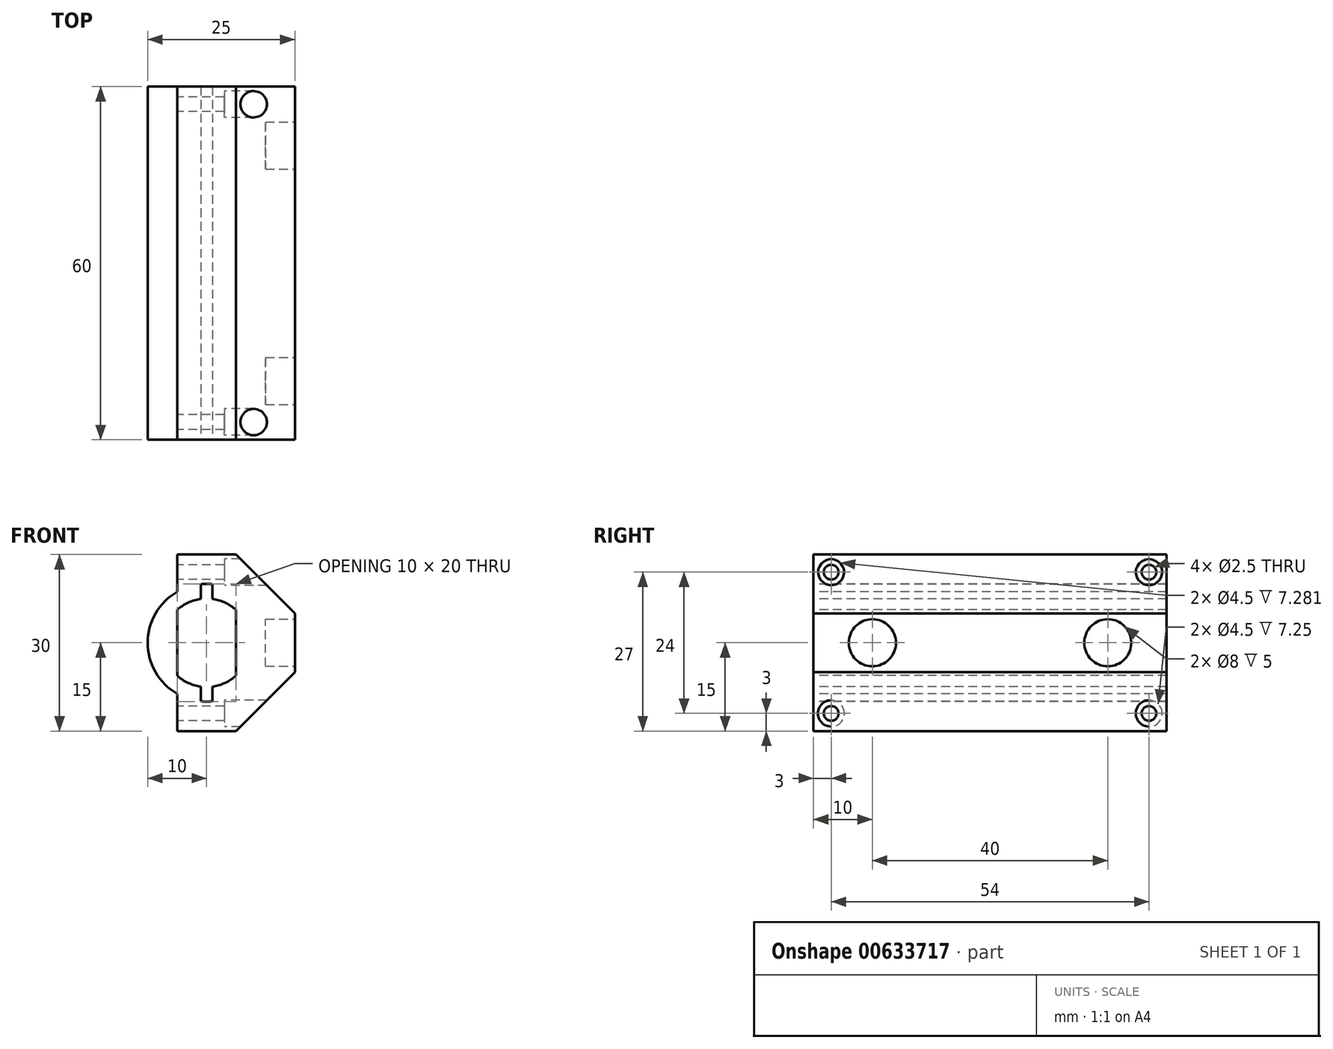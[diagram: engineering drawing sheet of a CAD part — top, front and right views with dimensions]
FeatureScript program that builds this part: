
annotation { "Feature Type Name" : "Feature", "Feature Type Description" : "" }
export const myFeature = defineFeature(function(context is Context, id is Id, definition is map)
    precondition{}
    {
        {
            var Q0;
            Q0=qCreatedBy(makeId("Right.planeOp"),FACE);
            var sketch = newSketch(context, id + "F0", { "sketchPlane" : qUnion([Q0])});
            skCircle(sketch, "E0", {"center": v(0, 0) * mm, "radius": 4 * mm});
            skSolve(sketch);
        }
        {
            var Q0;
            Q0 = qSketchRegion(id + "F0", true);
            extrude(context, id + "F1", {"entities" : qUnion([Q0]), "depth" : 200 * mm, "offsetDistance" : 25 * mm});
        }
        {
            var Q0;
            Q0=makeQuery(id+"F1.opExtrude","SWEPT_BODY",BODY,{"disambiguationData":[OSD([sQuery(id+"F0.wireOp",EDGE,"E0")])]});
            transform(context, id + "F2", {"entities" : qUnion([Q0]), "transformType" : TransformType.TRANSLATION_3D, "dx" : 0 * mm, "dy" : -40 * mm, "dz" : 0 * mm, "makeCopy" : true});
        }
        {
            var Q0;
            Q0=makeQuery(id+"F2.opPattern","COPY",FACE,{"derivedFrom":makeQuery(id+"F1.opExtrude","CAP_FACE",FACE,{"disambiguationData":[OSD([sQuery(id+"F0.wireOp",EDGE,"E0")])],"isStart":true}),"instanceName":"1"});
            var sketch = newSketch(context, id + "F3", { "sketchPlane" : qUnion([Q0])});
            skCircle(sketch, "E1", {"center": v(40, 0) * mm, "radius": 4 * mm});
            skCircle(sketch, "E2", {"center": v(0, 0) * mm, "radius": 4 * mm});
            skCircle(sketch, "E3", {"center": v(0, 0) * mm, "radius": 5 * mm});
            skCircle(sketch, "E4", {"center": v(40, 0) * mm, "radius": 5 * mm});
            skLineSegment(sketch, "E5", {"start": v(0, 0) * mm, "end": v(40, 0) * mm, "construction": true});
            skLineSegment(sketch, "E6", {"start": v(40, 5) * mm, "end": v(0, 5) * mm, "construction": true});
            skLineSegment(sketch, "E7", {"start": v(0, 5) * mm, "end": v(0, -5) * mm, "construction": true});
            skLineSegment(sketch, "E8", {"start": v(0, -5) * mm, "end": v(40, -5) * mm, "construction": true});
            skLineSegment(sketch, "E9", {"start": v(20, 5) * mm, "end": v(20, -5) * mm, "construction": true});
            skLineSegment(sketch, "E10.bottom", {"start": v(50, -15) * mm, "end": v(-10, -15) * mm});
            skLineSegment(sketch, "E10.top", {"start": v(50, 15) * mm, "end": v(-10, 15) * mm});
            skLineSegment(sketch, "E10.left", {"start": v(50, -15) * mm, "end": v(50, 15) * mm});
            skLineSegment(sketch, "E10.right", {"start": v(-10, -15) * mm, "end": v(-10, 15) * mm});
            skPoint(sketch, "E10.middle", {"position": v(20, 0) * mm});
            skSolve(sketch);
        }
        {
            var Q0;
            Q0=makeQuery(id+"F3.imprint","IMPRINT",FACE,{"disambiguationData":[TD([[makeQuery(id+"F3.imprint","IMPRINT",EDGE,{"derivedFrom":sQuery(id+"F3.wireOp",EDGE,"E1")}),1.0]])]});
            var Q1;
            Q1=makeQuery(id+"F3.imprint","IMPRINT",FACE,{"disambiguationData":[TD([[makeQuery(id+"F3.imprint","IMPRINT",EDGE,{"derivedFrom":sQuery(id+"F3.wireOp",EDGE,"E2")}),-1.0]])]});
            var Q2;
            Q2=sQuery(id+"F3.wireOp",EDGE,"E4");
            extrude(context, id + "F4", {"entities" : qUnion([Q0, Q1]), "surfaceEntities" : qUnion([Q2]), "oppositeDirection" : true, "depth" : 5 * mm, "offsetDistance" : 25 * mm});
        }
        {
            var Q0;
            Q0 = qSketchRegion(id + "F3", true);
            var Q1;
            Q1=makeQuery(id+"F4.opExtrude","CAP_FACE",FACE,{"disambiguationData":[OSD([sQuery(id+"F3.wireOp",EDGE,"E2"),sQuery(id+"F3.wireOp",EDGE,"E3")])],"isStart":true});
            var Q2;
            Q2=makeQuery(id+"F1.opExtrude","CAP_FACE",FACE,{"disambiguationData":[OSD([sQuery(id+"F0.wireOp",EDGE,"E0")])],"isStart":true});
            var Q3;
            Q3=makeQuery(id+"F2.opPattern","COPY",FACE,{"derivedFrom":makeQuery(id+"F1.opExtrude","CAP_FACE",FACE,{"disambiguationData":[OSD([sQuery(id+"F0.wireOp",EDGE,"E0")])],"isStart":true}),"instanceName":"1"});
            var Q4;
            Q4=makeQuery(id+"F4.opExtrude","CAP_FACE",FACE,{"disambiguationData":[OSD([sQuery(id+"F3.wireOp",EDGE,"E1"),sQuery(id+"F3.wireOp",EDGE,"E4")])],"isStart":true});
            extrude(context, id + "F5", {"entities" : qUnion([Q0, Q1, Q2, Q3, Q4]), "operationType" : NewBodyOperationType.ADD, "depth" : 30 * mm, "offsetDistance" : 25 * mm});
        }
        {
            var Q0;
            Q0=makeQuery(id+"F5.opExtrude","SWEPT_FACE",FACE,{"disambiguationData":[OSD([sQuery(id+"F3.wireOp",EDGE,"E10.left")])]});
            var sketch = newSketch(context, id + "F6", { "sketchPlane" : qUnion([Q0])});
            skCircle(sketch, "E11", {"center": v(-15, 0) * mm, "radius": 7.5 * mm});
            skPoint(sketch, "E11.centerSnap0", {"position": v(-15, 15) * mm});
            skCircle(sketch, "E12", {"center": v(-15, 0) * mm, "radius": 10 * mm});
            skLineSegment(sketch, "E13.bottom", {"start": v(-10, -15) * mm, "end": v(-20, -15) * mm});
            skLineSegment(sketch, "E13.top", {"start": v(-10, 15) * mm, "end": v(-20, 15) * mm});
            skLineSegment(sketch, "E13.left", {"start": v(-10, -15) * mm, "end": v(-10, 15) * mm});
            skLineSegment(sketch, "E13.right", {"start": v(-20, -15) * mm, "end": v(-20, 15) * mm});
            skLineSegment(sketch, "E14.bottom", {"start": v(-14, 15) * mm, "end": v(-16, 15) * mm});
            skLineSegment(sketch, "E14.top", {"start": v(-14, -15) * mm, "end": v(-16, -15) * mm});
            skLineSegment(sketch, "E14.left", {"start": v(-14, 15) * mm, "end": v(-14, -15) * mm});
            skLineSegment(sketch, "E14.right", {"start": v(-16, 15) * mm, "end": v(-16, -15) * mm});
            skSolve(sketch);
        }
        {
            var Q0;
            Q0=makeQuery(id+"F6.imprint","IMPRINT",FACE,{"disambiguationData":[TD([[makeQuery(id+"F6.imprint","IMPRINT",EDGE,{"derivedFrom":sQuery(id+"F6.wireOp",EDGE,"E11")}),1.0]])]});
            var Q1;
            {var subQ0=sQuery(id+"F6.wireOp",EDGE,"E13.left");var subQ1=sQuery(id+"F6.wireOp",EDGE,"E11");var subQ2=makeQuery(id+"F6.imprint","INTERSECT",VERTEX,{"disambiguationData":[OD(0.0)],"derivedFrom":[subQ1,subQ0]});Q1=makeQuery(id+"F6.imprint","IMPRINT",FACE,{"disambiguationData":[TD([[makeQuery(id+"F6.imprint","IMPRINT",EDGE,{"disambiguationData":[TD([[subQ2,1.0]])],"derivedFrom":subQ1}),1.0]])]});}
            var Q2;
            {var subQ0=sQuery(id+"F6.wireOp",EDGE,"E13.right");var subQ1=sQuery(id+"F6.wireOp",EDGE,"E11");var subQ2=makeQuery(id+"F6.imprint","INTERSECT",VERTEX,{"disambiguationData":[OD(0.0)],"derivedFrom":[subQ1,subQ0]});Q2=makeQuery(id+"F6.imprint","IMPRINT",FACE,{"disambiguationData":[TD([[makeQuery(id+"F6.imprint","IMPRINT",EDGE,{"disambiguationData":[TD([[subQ2,-1.0]])],"derivedFrom":subQ1}),1.0]])]});}
            var Q3;
            {var subQ5=sQuery(id+"F6.wireOp",EDGE,"E14.bottom");Q3=makeQuery(id+"F6.imprint","IMPRINT",FACE,{"disambiguationData":[TD([[makeQuery(id+"F6.imprint","IMPRINT",EDGE,{"derivedFrom":subQ5}),-1.0]])]});}
            var Q4;
            {var subQ0=sQuery(id+"F6.wireOp",EDGE,"E14.left");var subQ1=sQuery(id+"F6.wireOp",EDGE,"E11");var subQ2=makeQuery(id+"F6.imprint","INTERSECT",VERTEX,{"disambiguationData":[OD(0.0)],"derivedFrom":[subQ1,subQ0]});Q4=makeQuery(id+"F6.imprint","IMPRINT",FACE,{"disambiguationData":[TD([[makeQuery(id+"F6.imprint","IMPRINT",EDGE,{"disambiguationData":[TD([[subQ2,-1.0]])],"derivedFrom":subQ1}),-1.0]])]});}
            var Q5;
            {var subQ0=sQuery(id+"F6.wireOp",EDGE,"E14.right");var subQ1=sQuery(id+"F6.wireOp",EDGE,"E11");var subQ2=makeQuery(id+"F6.imprint","INTERSECT",VERTEX,{"disambiguationData":[OD(1.0)],"derivedFrom":[subQ1,subQ0]});Q5=makeQuery(id+"F6.imprint","IMPRINT",FACE,{"disambiguationData":[TD([[makeQuery(id+"F6.imprint","IMPRINT",EDGE,{"disambiguationData":[TD([[subQ2,-1.0]])],"derivedFrom":subQ1}),-1.0]])]});}
            var Q6;
            {var subQ5=sQuery(id+"F6.wireOp",EDGE,"E14.top");Q6=makeQuery(id+"F6.imprint","IMPRINT",FACE,{"disambiguationData":[TD([[makeQuery(id+"F6.imprint","IMPRINT",EDGE,{"derivedFrom":subQ5}),1.0]])]});}
            extrude(context, id + "F7", {"entities" : qUnion([Q0, Q1, Q2, Q3, Q4, Q5, Q6]), "operationType" : NewBodyOperationType.REMOVE, "endBound" : BoundingType.THROUGH_ALL, "oppositeDirection" : true, "depth" : 25 * mm, "offsetDistance" : 25 * mm});
        }
        {
            var Q0;
            {var subQ0=sQuery(id+"F3.wireOp",EDGE,"E10.left");var subQ1=makeQuery(id+"F5.opExtrude","CAP_EDGE",EDGE,{"disambiguationData":[OSD([subQ0])],"isStart":false});Q0=makeQuery(id+"F6.imprint","IMPRINT",FACE,{"disambiguationData":[TD([[makeQuery(id+"F6.imprint","IMPRINT",EDGE,{"derivedFrom":subQ1}),-1.0]])]});}
            extrude(context, id + "F8", {"entities" : qUnion([Q0]), "operationType" : NewBodyOperationType.REMOVE, "endBound" : BoundingType.THROUGH_ALL, "oppositeDirection" : true, "depth" : 25 * mm, "offsetDistance" : 25 * mm});
        }
        {
            var Q0;
            Q0=makeQuery(id+"F5.opExtrude","CAP_EDGE",EDGE,{"disambiguationData":[OSD([sQuery(id+"F3.wireOp",EDGE,"E10.top")])],"isStart":true});
            var Q1;
            Q1=makeQuery(id+"F5.opExtrude","CAP_EDGE",EDGE,{"disambiguationData":[OSD([sQuery(id+"F3.wireOp",EDGE,"E10.bottom")])],"isStart":true});
            chamfer(context, id + "F9", {"entities" : qUnion([Q0, Q1]), "width" : 10 * mm, "tangentPropagation" : true});
        }
        {
            var Q0;
            {var subQ0=sQuery(id+"F6.wireOp",EDGE,"E13.right");Q0=makeQuery(id+"F8.boolean.opBoolean","COPY",FACE,{"derivedFrom":makeQuery(id+"F8.opExtrude","SWEPT_FACE",FACE,{"disambiguationData":[OSD([subQ0]),TDD([makeQuery(id+"F6.imprint","IMPRINT",EDGE,{"disambiguationData":[TD([[makeQuery(id+"F6.imprint","INTERSECT",VERTEX,{"disambiguationData":[OD(0.0)],"derivedFrom":[sQuery(id+"F6.wireOp",EDGE,"E12"),subQ0]}),-1.0]])],"derivedFrom":subQ0})])]})});}
            var sketch = newSketch(context, id + "F10", { "sketchPlane" : qUnion([Q0])});
            skLineSegment(sketch, "E15.0", {"start": v(-7, -8.66) * mm, "end": v(-7, -12) * mm});
            skLineSegment(sketch, "E15.1", {"start": v(-7, 12) * mm, "end": v(-7, 8.66) * mm});
            skLineSegment(sketch, "E15.2", {"start": v(-7, 12) * mm, "end": v(47, 12) * mm});
            skLineSegment(sketch, "E15.3", {"start": v(47, 12) * mm, "end": v(47, -12) * mm});
            skLineSegment(sketch, "E15.4", {"start": v(-7, -12) * mm, "end": v(47, -12) * mm});
            skCircle(sketch, "E16", {"center": v(-7, 12) * mm, "radius": 1.25 * mm});
            skCircle(sketch, "E17", {"center": v(47, 12) * mm, "radius": 1.25 * mm});
            skCircle(sketch, "E18", {"center": v(47, -12) * mm, "radius": 1.25 * mm});
            skCircle(sketch, "E19", {"center": v(-7, -12) * mm, "radius": 1.25 * mm});
            skSolve(sketch);
        }
        {
            var Q0;
            {var subQ0=sQuery(id+"F10.wireOp",EDGE,"E15.2");var subQ1=sQuery(id+"F10.wireOp",EDGE,"E15.1");var subQ2=makeQuery(id+"F10.imprint","INTERSECT",VERTEX,{"derivedFrom":[subQ1,subQ0]});Q0=makeQuery(id+"F10.imprint","IMPRINT",FACE,{"disambiguationData":[TD([[makeQuery(id+"F10.imprint","IMPRINT",EDGE,{"disambiguationData":[TD([[subQ2,-1.0]])],"derivedFrom":subQ1}),1.0]])]});}
            var Q1;
            {var subQ0=sQuery(id+"F10.wireOp",EDGE,"E15.2");var subQ1=sQuery(id+"F10.wireOp",EDGE,"E15.1");var subQ2=makeQuery(id+"F10.imprint","INTERSECT",VERTEX,{"derivedFrom":[subQ1,subQ0]});Q1=makeQuery(id+"F10.imprint","IMPRINT",FACE,{"disambiguationData":[TD([[makeQuery(id+"F10.imprint","IMPRINT",EDGE,{"disambiguationData":[TD([[subQ2,-1.0]])],"derivedFrom":subQ1}),-1.0]])]});}
            var Q2;
            {var subQ0=sQuery(id+"F10.wireOp",EDGE,"E15.3");var subQ1=sQuery(id+"F10.wireOp",EDGE,"E15.2");var subQ2=makeQuery(id+"F10.imprint","INTERSECT",VERTEX,{"derivedFrom":[subQ1,subQ0]});Q2=makeQuery(id+"F10.imprint","IMPRINT",FACE,{"disambiguationData":[TD([[makeQuery(id+"F10.imprint","IMPRINT",EDGE,{"disambiguationData":[TD([[subQ2,1.0]])],"derivedFrom":subQ1}),-1.0]])]});}
            var Q3;
            {var subQ0=sQuery(id+"F10.wireOp",EDGE,"E15.3");var subQ1=sQuery(id+"F10.wireOp",EDGE,"E15.2");var subQ2=makeQuery(id+"F10.imprint","INTERSECT",VERTEX,{"derivedFrom":[subQ1,subQ0]});Q3=makeQuery(id+"F10.imprint","IMPRINT",FACE,{"disambiguationData":[TD([[makeQuery(id+"F10.imprint","IMPRINT",EDGE,{"disambiguationData":[TD([[subQ2,1.0]])],"derivedFrom":subQ1}),1.0]])]});}
            var Q4;
            {var subQ0=sQuery(id+"F10.wireOp",EDGE,"E15.4");var subQ1=sQuery(id+"F10.wireOp",EDGE,"E15.3");var subQ2=makeQuery(id+"F10.imprint","INTERSECT",VERTEX,{"derivedFrom":[subQ1,subQ0]});Q4=makeQuery(id+"F10.imprint","IMPRINT",FACE,{"disambiguationData":[TD([[makeQuery(id+"F10.imprint","IMPRINT",EDGE,{"disambiguationData":[TD([[subQ2,1.0]])],"derivedFrom":subQ1}),-1.0]])]});}
            var Q5;
            {var subQ0=sQuery(id+"F10.wireOp",EDGE,"E15.4");var subQ1=sQuery(id+"F10.wireOp",EDGE,"E15.3");var subQ2=makeQuery(id+"F10.imprint","INTERSECT",VERTEX,{"derivedFrom":[subQ1,subQ0]});Q5=makeQuery(id+"F10.imprint","IMPRINT",FACE,{"disambiguationData":[TD([[makeQuery(id+"F10.imprint","IMPRINT",EDGE,{"disambiguationData":[TD([[subQ2,1.0]])],"derivedFrom":subQ1}),1.0]])]});}
            var Q6;
            {var subQ0=sQuery(id+"F10.wireOp",EDGE,"E15.4");var subQ1=sQuery(id+"F10.wireOp",EDGE,"E15.0");var subQ2=makeQuery(id+"F10.imprint","INTERSECT",VERTEX,{"derivedFrom":[subQ1,subQ0]});Q6=makeQuery(id+"F10.imprint","IMPRINT",FACE,{"disambiguationData":[TD([[makeQuery(id+"F10.imprint","IMPRINT",EDGE,{"disambiguationData":[TD([[subQ2,1.0]])],"derivedFrom":subQ1}),1.0]])]});}
            var Q7;
            {var subQ0=sQuery(id+"F10.wireOp",EDGE,"E15.4");var subQ1=sQuery(id+"F10.wireOp",EDGE,"E15.0");var subQ2=makeQuery(id+"F10.imprint","INTERSECT",VERTEX,{"derivedFrom":[subQ1,subQ0]});Q7=makeQuery(id+"F10.imprint","IMPRINT",FACE,{"disambiguationData":[TD([[makeQuery(id+"F10.imprint","IMPRINT",EDGE,{"disambiguationData":[TD([[subQ2,1.0]])],"derivedFrom":subQ1}),-1.0]])]});}
            extrude(context, id + "F11", {"entities" : qUnion([Q0, Q1, Q2, Q3, Q4, Q5, Q6, Q7]), "operationType" : NewBodyOperationType.REMOVE, "oppositeDirection" : true, "depth" : 25 * mm, "offsetDistance" : 25 * mm});
        }
        {
            var Q0;
            {var subQ0=sQuery(id+"F6.wireOp",EDGE,"E14.left");var subQ1=makeQuery(id+"F6.imprint","INTERSECT",VERTEX,{"disambiguationData":[OD(0.0)],"derivedFrom":[sQuery(id+"F6.wireOp",EDGE,"E12"),subQ0]});Q0=makeQuery(id+"F7.boolean.opBoolean","COPY",FACE,{"derivedFrom":makeQuery(id+"F7.opExtrude","SWEPT_FACE",FACE,{"disambiguationData":[OSD([subQ0]),TDD([makeQuery(id+"F6.imprint","IMPRINT",EDGE,{"disambiguationData":[TD([[subQ1,1.0]])],"derivedFrom":subQ0}),makeQuery(id+"F6.imprint","IMPRINT",EDGE,{"disambiguationData":[TD([[makeQuery(id+"F6.imprint","INTERSECT",VERTEX,{"disambiguationData":[OD(0.0)],"derivedFrom":[sQuery(id+"F6.wireOp",EDGE,"E11"),subQ0]}),1.0]])],"derivedFrom":subQ0})])]})});}
            var sketch = newSketch(context, id + "F12", { "sketchPlane" : qUnion([Q0])});
            skCircle(sketch, "E20.0", {"center": v(47, 12) * mm, "radius": 2.25 * mm});
            skCircle(sketch, "E21.0", {"center": v(-7, 12) * mm, "radius": 2.25 * mm});
            skCircle(sketch, "E22.0", {"center": v(47, -12) * mm, "radius": 2.25 * mm});
            skCircle(sketch, "E23.0", {"center": v(-7, -12) * mm, "radius": 2.25 * mm});
            skSolve(sketch);
        }
        {
            var Q0;
            Q0=makeQuery(id+"F12.imprint","IMPRINT",FACE,{"disambiguationData":[TD([[makeQuery(id+"F12.imprint","IMPRINT",EDGE,{"derivedFrom":sQuery(id+"F12.wireOp",EDGE,"E20.0")}),1.0]])]});
            var Q1;
            Q1=makeQuery(id+"F12.imprint","IMPRINT",FACE,{"disambiguationData":[TD([[makeQuery(id+"F12.imprint","IMPRINT",EDGE,{"derivedFrom":sQuery(id+"F12.wireOp",EDGE,"E22.0")}),1.0]])]});
            var Q2;
            Q2=makeQuery(id+"F12.imprint","IMPRINT",FACE,{"disambiguationData":[TD([[makeQuery(id+"F12.imprint","IMPRINT",EDGE,{"derivedFrom":sQuery(id+"F12.wireOp",EDGE,"E23.0")}),1.0]])]});
            var Q3;
            Q3=makeQuery(id+"F12.imprint","IMPRINT",FACE,{"disambiguationData":[TD([[makeQuery(id+"F12.imprint","IMPRINT",EDGE,{"derivedFrom":sQuery(id+"F12.wireOp",EDGE,"E21.0")}),1.0]])]});
            extrude(context, id + "F13", {"entities" : qUnion([Q0, Q1, Q2, Q3]), "operationType" : NewBodyOperationType.REMOVE, "oppositeDirection" : true, "depth" : 25 * mm, "offsetDistance" : 25 * mm, "hasSecondDirection" : true, "secondDirectionOppositeDirection" : false, "secondDirectionDepth" : -2 * mm});
        }
        {
            var Q0;
            Q0=makeQuery(id+"F2.opPattern","COPY",FACE,{"derivedFrom":makeQuery(id+"F1.opExtrude","CAP_FACE",FACE,{"disambiguationData":[OSD([sQuery(id+"F0.wireOp",EDGE,"E0")])],"isStart":false}),"instanceName":"1"});
            var Q1;
            Q1=makeQuery(id+"F1.opExtrude","CAP_FACE",FACE,{"disambiguationData":[OSD([sQuery(id+"F0.wireOp",EDGE,"E0")])],"isStart":false});
            var Q2;
            {var subQ0=sQuery(id+"F3.wireOp",EDGE,"E3");var subQ1=sQuery(id+"F3.wireOp",EDGE,"E4");var subQ2=sQuery(id+"F0.wireOp",EDGE,"E0");var subQ3=makeQuery(id+"F1.opExtrude","CAP_FACE",FACE,{"disambiguationData":[OSD([subQ2])],"isStart":true});Q2=makeQuery(id+"F9.opChamfer","SPLIT",FACE,{"disambiguationData":[OD(0.0)],"derivedFrom":makeQuery(id+"F5.boolean.opBoolean","MERGE",FACE,{"derivedFrom":[makeQuery(id+"F5.opExtrude","CAP_FACE",FACE,{"disambiguationData":[OSD([subQ2]),TDD([subQ3])],"isStart":true}),makeQuery(id+"F5.opExtrude","CAP_FACE",FACE,{"disambiguationData":[OSD([subQ2]),TDD([makeQuery(id+"F2.opPattern","COPY",FACE,{"derivedFrom":subQ3,"instanceName":"1"})])],"isStart":true}),makeQuery(id+"F5.opExtrude","CAP_FACE",FACE,{"disambiguationData":[OSD([subQ0,subQ1,sQuery(id+"F3.wireOp",EDGE,"E10.bottom"),sQuery(id+"F3.wireOp",EDGE,"E10.top"),sQuery(id+"F3.wireOp",EDGE,"E10.left"),sQuery(id+"F3.wireOp",EDGE,"E10.right")])],"isStart":true}),makeQuery(id+"F5.opExtrude","CAP_FACE",FACE,{"disambiguationData":[OSD([sQuery(id+"F3.wireOp",EDGE,"E1"),subQ1])],"isStart":true}),makeQuery(id+"F5.opExtrude","CAP_FACE",FACE,{"disambiguationData":[OSD([sQuery(id+"F3.wireOp",EDGE,"E2"),subQ0])],"isStart":true})]})});}
            extrude(context, id + "F14", {"entities" : qUnion([Q0, Q1]), "operationType" : NewBodyOperationType.REMOVE, "endBound" : BoundingType.UP_TO_SURFACE, "oppositeDirection" : true, "depth" : 148.3 * mm, "endBoundEntityFace" : qUnion([Q2]), "offsetDistance" : 25 * mm});
        }
        {
            var Q0;
            {var subQ0=sQuery(id+"F0.wireOp",EDGE,"E0");Q0=makeQuery(id+"F14.boolean.opBoolean","COPY",FACE,{"derivedFrom":makeQuery(id+"F14.opExtrude","CAP_FACE",FACE,{"disambiguationData":[OSD([subQ0]),TDD([makeQuery(id+"F2.opPattern","COPY",FACE,{"derivedFrom":makeQuery(id+"F1.opExtrude","CAP_FACE",FACE,{"disambiguationData":[OSD([subQ0])],"isStart":false}),"instanceName":"1"})])],"isStart":false})});}
            var Q1;
            {var subQ0=sQuery(id+"F0.wireOp",EDGE,"E0");Q1=makeQuery(id+"F14.boolean.opBoolean","COPY",FACE,{"derivedFrom":makeQuery(id+"F14.opExtrude","CAP_FACE",FACE,{"disambiguationData":[OSD([subQ0]),TDD([makeQuery(id+"F1.opExtrude","CAP_FACE",FACE,{"disambiguationData":[OSD([subQ0])],"isStart":false})])],"isStart":false})});}
            var Q2;
            Q2=makeQuery(id+"F4.opExtrude","CAP_FACE",FACE,{"disambiguationData":[OSD([sQuery(id+"F3.wireOp",EDGE,"E1"),sQuery(id+"F3.wireOp",EDGE,"E4")])],"isStart":false});
            var Q3;
            Q3=makeQuery(id+"F4.opExtrude","CAP_FACE",FACE,{"disambiguationData":[OSD([sQuery(id+"F3.wireOp",EDGE,"E2"),sQuery(id+"F3.wireOp",EDGE,"E3")])],"isStart":false});
            extrude(context, id + "F15", {"entities" : qUnion([Q0, Q1, Q2, Q3]), "operationType" : NewBodyOperationType.REMOVE, "oppositeDirection" : true, "depth" : 5 * mm, "offsetDistance" : 25 * mm});
        }
    });
